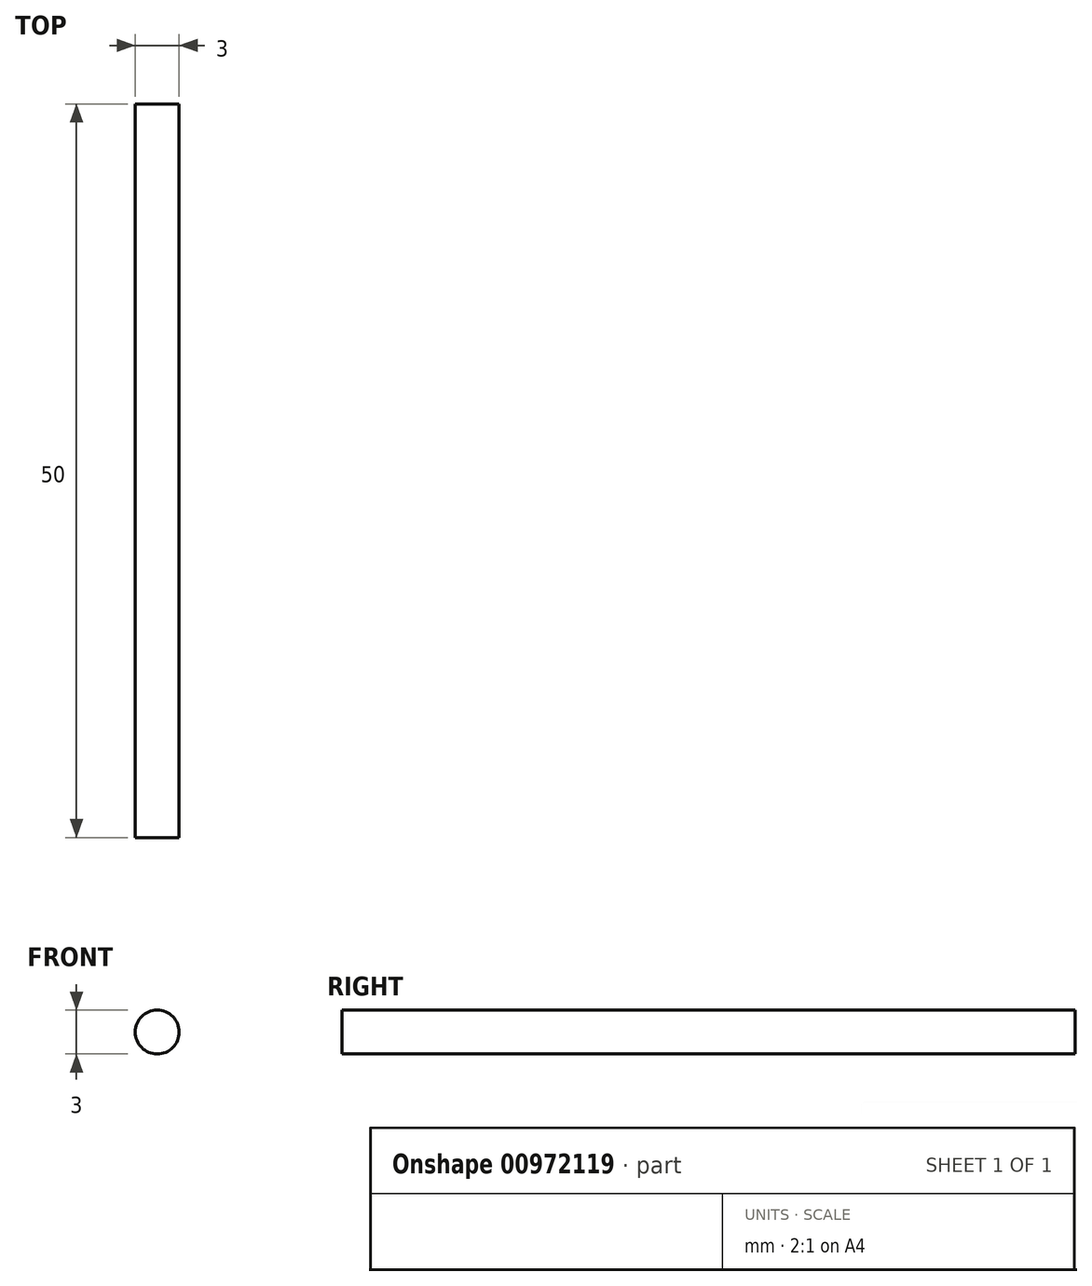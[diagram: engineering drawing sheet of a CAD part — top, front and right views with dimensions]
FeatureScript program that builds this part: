
annotation { "Feature Type Name" : "Feature", "Feature Type Description" : "" }
export const myFeature = defineFeature(function(context is Context, id is Id, definition is map)
    precondition{}
    {
        {
            var Q0;
            Q0=qCreatedBy(makeId("Front.planeOp"),FACE);
            var sketch = newSketch(context, id + "F0", { "sketchPlane" : qUnion([Q0])});
            skCircle(sketch, "E0", {"center": v(0, 0) * mm, "radius": 1.5 * mm});
            skSolve(sketch);
        }
        {
            var Q0;
            Q0=makeQuery(id+"F0.imprint","IMPRINT",FACE,{"disambiguationData":[TD([[makeQuery(id+"F0.imprint","IMPRINT",EDGE,{"derivedFrom":sQuery(id+"F0.wireOp",EDGE,"E0")}),1.0]])]});
            extrude(context, id + "F1", {"entities" : qUnion([Q0]), "depth" : 50 * mm, "offsetDistance" : 25 * mm});
        }
    });
